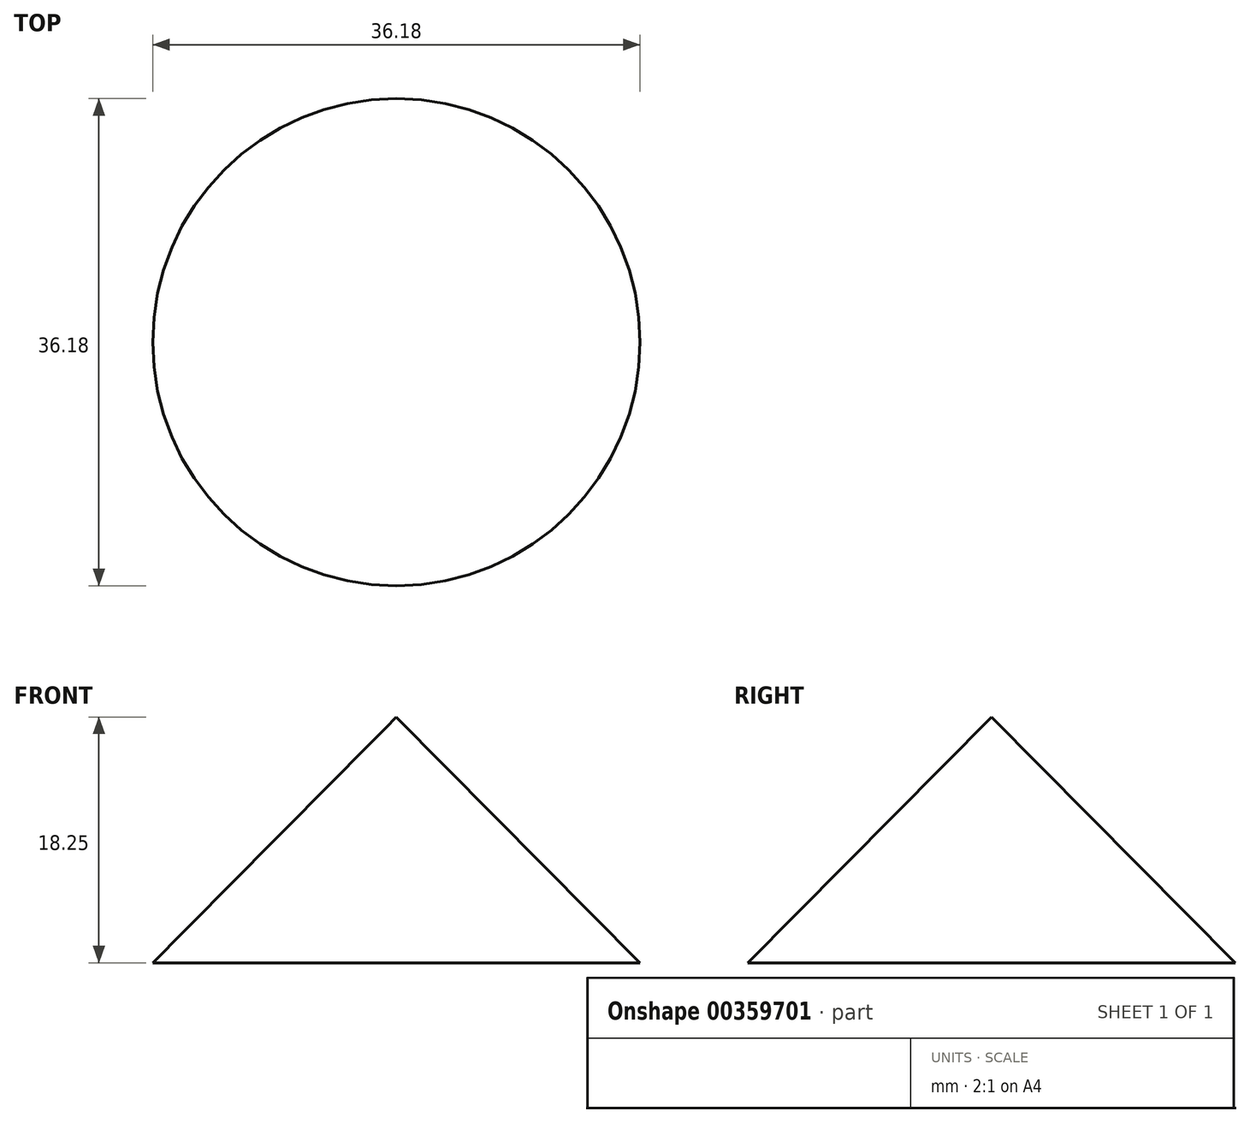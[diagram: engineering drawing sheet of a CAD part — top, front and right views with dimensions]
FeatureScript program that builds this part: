
annotation { "Feature Type Name" : "Feature", "Feature Type Description" : "" }
export const myFeature = defineFeature(function(context is Context, id is Id, definition is map)
    precondition{}
    {
        {
            var Q0;
            Q0=qCreatedBy(makeId("Front.planeOp"),FACE);
            var sketch = newSketch(context, id + "F0", { "sketchPlane" : qUnion([Q0])});
            skLineSegment(sketch, "E0", {"start": v(-32.7, 49.28) * mm, "end": v(-50.79, 31.03) * mm});
            skLineSegment(sketch, "E1", {"start": v(-50.79, 31.03) * mm, "end": v(-32.7, 31.03) * mm});
            skLineSegment(sketch, "E2", {"start": v(-32.7, 31.03) * mm, "end": v(-32.7, 49.28) * mm});
            skSolve(sketch);
        }
        {
            var Q0;
            Q0=makeQuery(id+"F0.imprint","IMPRINT",FACE,{"disambiguationData":[TD([[makeQuery(id+"F0.imprint","IMPRINT",EDGE,{"derivedFrom":sQuery(id+"F0.wireOp",EDGE,"E0")}),1.0]])]});
            var Q1;
            Q1=sQuery(id+"F0.wireOp",EDGE,"E2");
            revolve(context, id + "F1", {"entities" : qUnion([Q0]), "axis" : qUnion([Q1]), "revolveType" : RevolveType.FULL});
        }
    });
